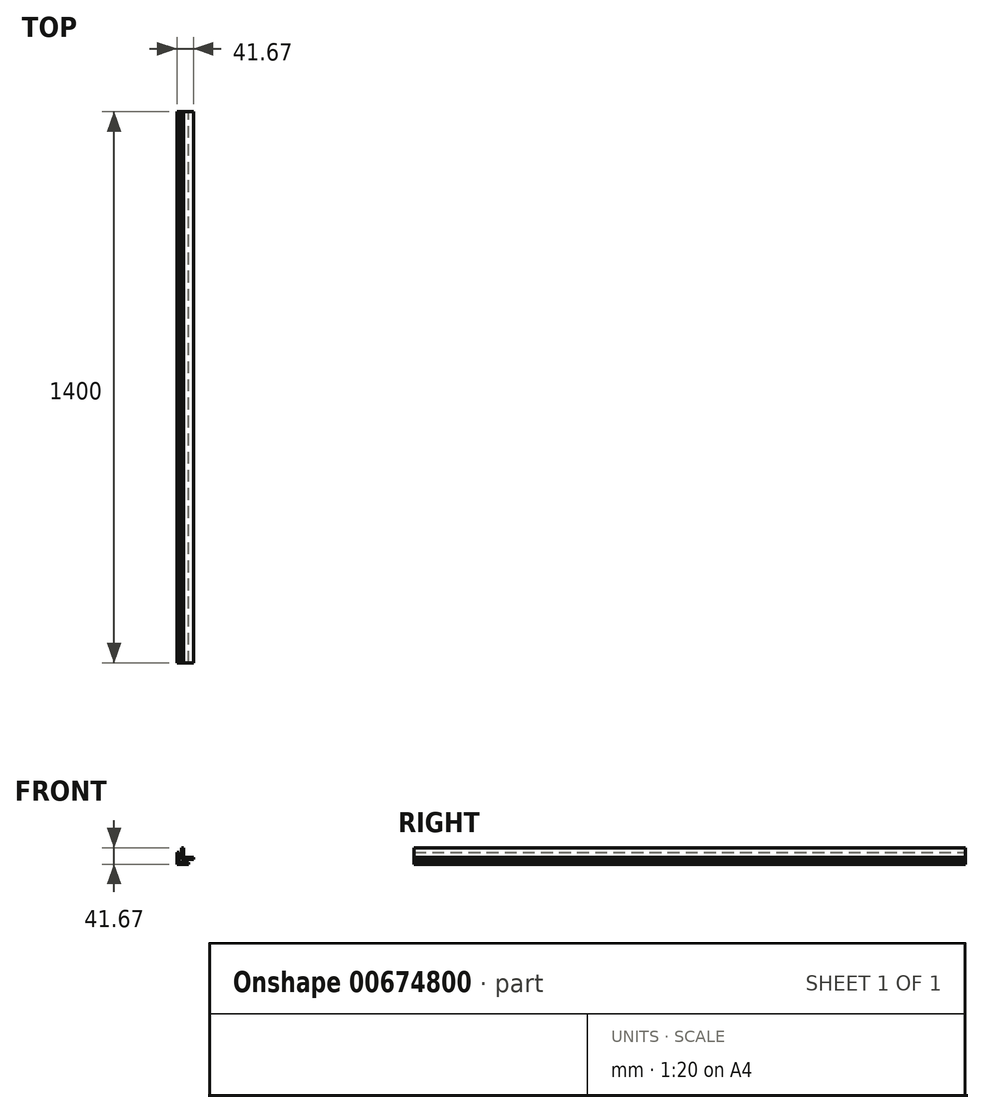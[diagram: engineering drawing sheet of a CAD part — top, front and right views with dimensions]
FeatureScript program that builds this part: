
annotation { "Feature Type Name" : "Feature", "Feature Type Description" : "" }
export const myFeature = defineFeature(function(context is Context, id is Id, definition is map)
    precondition{}
    {
        {
            var Q0;
            Q0=qCreatedBy(makeId("Front.planeOp"),FACE);
            var sketch = newSketch(context, id + "F0", { "sketchPlane" : qUnion([Q0])});
            skLineSegment(sketch, "E0", {"start": v(0, 0) * mm, "end": v(0, 30) * mm});
            skLineSegment(sketch, "E1", {"start": v(0, 0) * mm, "end": v(30, 0) * mm});
            skLineSegment(sketch, "E2", {"start": v(0, 30) * mm, "end": v(5, 30) * mm});
            skLineSegment(sketch, "E3", {"start": v(30, 0) * mm, "end": v(30, 5) * mm});
            skLineSegment(sketch, "E4", {"start": v(30, 5) * mm, "end": v(5, 5) * mm});
            skLineSegment(sketch, "E5", {"start": v(5, 5) * mm, "end": v(5, 30) * mm});
            skLineSegment(sketch, "E6", {"start": v(-11.67, -11.67) * mm, "end": v(-11.67, 18.33) * mm});
            skLineSegment(sketch, "E7", {"start": v(-11.67, -11.67) * mm, "end": v(18.33, -11.67) * mm});
            skLineSegment(sketch, "E8", {"start": v(-11.67, 18.33) * mm, "end": v(-6.67, 18.33) * mm});
            skLineSegment(sketch, "E9", {"start": v(18.33, -11.67) * mm, "end": v(18.33, -6.67) * mm});
            skLineSegment(sketch, "E10", {"start": v(18.33, -6.67) * mm, "end": v(-6.67, -6.67) * mm});
            skLineSegment(sketch, "E11", {"start": v(-6.67, -6.67) * mm, "end": v(-6.67, 18.33) * mm});
            skSolve(sketch);
        }
        {
            var Q0;
            Q0=makeQuery(id+"F0.imprint","IMPRINT",FACE,{"disambiguationData":[TD([[makeQuery(id+"F0.imprint","IMPRINT",EDGE,{"derivedFrom":sQuery(id+"F0.wireOp",EDGE,"E6")}),-1.0]])]});
            var Q1;
            Q1=makeQuery(id+"F0.imprint","IMPRINT",FACE,{"disambiguationData":[TD([[makeQuery(id+"F0.imprint","IMPRINT",EDGE,{"derivedFrom":sQuery(id+"F0.wireOp",EDGE,"E0")}),-1.0]])]});
            extrude(context, id + "F1", {"entities" : qUnion([Q0, Q1]), "depth" : 1400 * mm, "offsetDistance" : 25 * mm});
        }
    });
